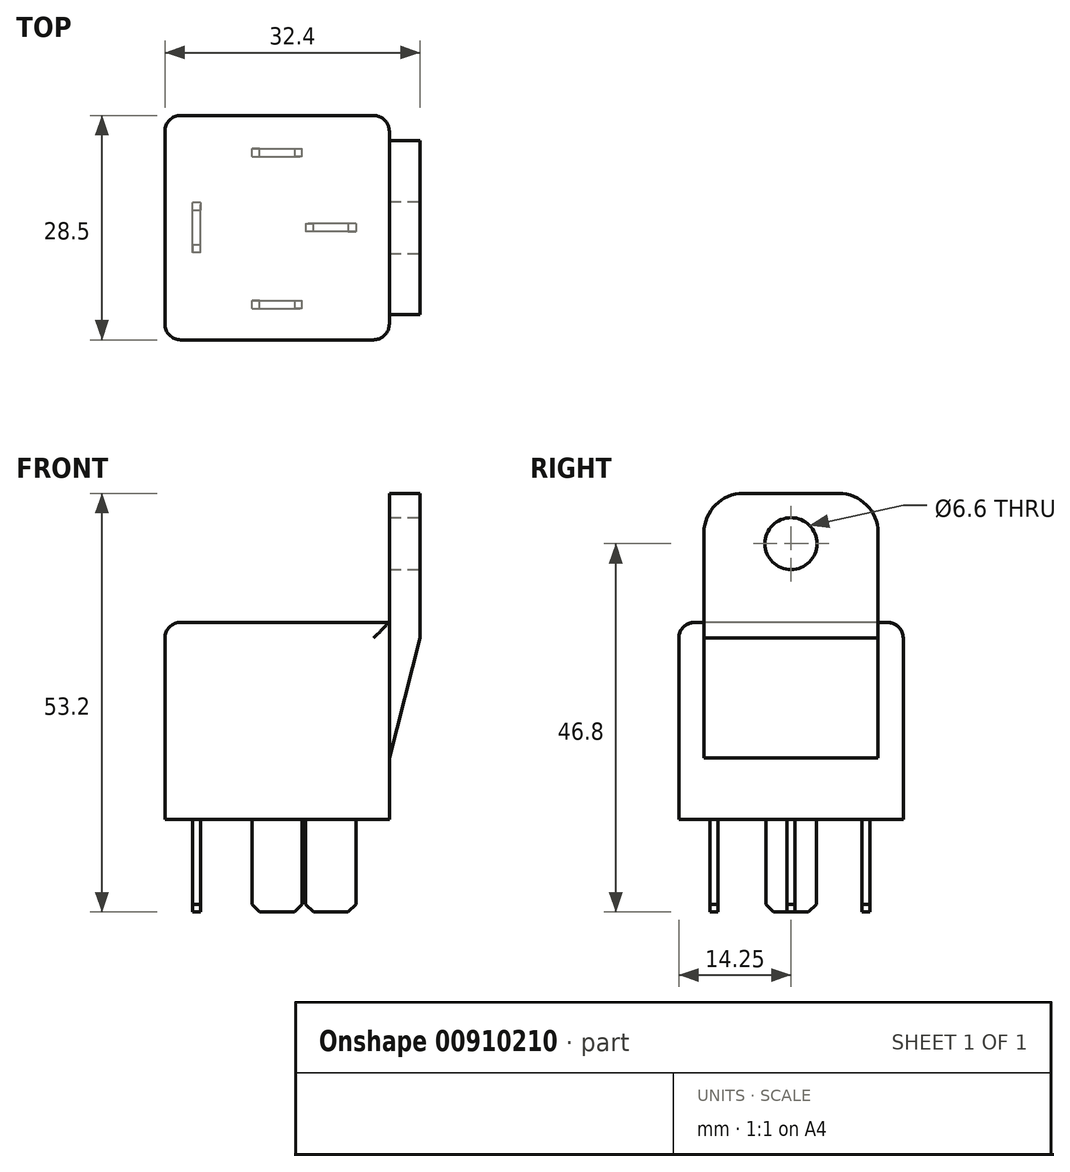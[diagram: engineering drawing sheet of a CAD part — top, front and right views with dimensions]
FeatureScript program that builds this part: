
annotation { "Feature Type Name" : "Feature", "Feature Type Description" : "" }
export const myFeature = defineFeature(function(context is Context, id is Id, definition is map)
    precondition{}
    {
        {
            var Q0;
            Q0=qCreatedBy(makeId("Top.planeOp"),FACE);
            var sketch = newSketch(context, id + "F0", { "sketchPlane" : qUnion([Q0])});
            skLineSegment(sketch, "E0.bottom", {"start": v(-14.25, 14.25) * mm, "end": v(14.25, 14.25) * mm});
            skLineSegment(sketch, "E0.top", {"start": v(-14.25, -14.25) * mm, "end": v(14.25, -14.25) * mm});
            skLineSegment(sketch, "E0.left", {"start": v(-14.25, 14.25) * mm, "end": v(-14.25, -14.25) * mm});
            skLineSegment(sketch, "E0.right", {"start": v(14.25, 14.25) * mm, "end": v(14.25, -14.25) * mm});
            skPoint(sketch, "E0.middle", {"position": v(0, 0) * mm});
            skSolve(sketch);
        }
        {
            var Q0;
            Q0 = qSketchRegion(id + "F0", true);
            extrude(context, id + "F1", {"entities" : qUnion([Q0]), "depth" : 25 * mm, "offsetDistance" : 25 * mm});
        }
        {
            var Q0;
            Q0=makeQuery(id+"F1.opExtrude","SWEPT_FACE",FACE,{"disambiguationData":[OSD([sQuery(id+"F0.wireOp",EDGE,"E0.top")])]});
            var sketch = newSketch(context, id + "F2", { "sketchPlane" : qUnion([Q0])});
            skLineSegment(sketch, "E1", {"start": v(14.25, 23) * mm, "end": v(18.15, 23) * mm});
            skLineSegment(sketch, "E2", {"start": v(18.15, 23) * mm, "end": v(14.25, 7.8) * mm});
            skSolve(sketch);
        }
        {
            var Q0;
            Q0 = qSketchRegion(id + "F2", true);
            var Q1;
            {var subQ0=sQuery(id+"F2.wireOp",EDGE,"E1");Q1=makeQuery(id+"F2.imprint","IMPRINT",FACE,{"disambiguationData":[TD([[makeQuery(id+"F2.imprint","IMPRINT",EDGE,{"derivedFrom":subQ0}),-1.0]])]});}
            extrude(context, id + "F3", {"entities" : qUnion([Q0, Q1]), "operationType" : NewBodyOperationType.ADD, "oppositeDirection" : true, "depth" : 25.3 * mm, "offsetDistance" : 25 * mm, "hasSecondDirection" : true, "secondDirectionOppositeDirection" : false, "secondDirectionDepth" : -3.2 * mm});
        }
        {
            var Q0;
            Q0=makeQuery(id+"F3.opExtrude","SWEPT_FACE",FACE,{"disambiguationData":[OSD([sQuery(id+"F2.wireOp",EDGE,"E1")])]});
            extrude(context, id + "F4", {"entities" : qUnion([Q0]), "operationType" : NewBodyOperationType.ADD, "depth" : 18.4 * mm, "offsetDistance" : 25 * mm});
        }
        {
            var Q0;
            {var subQ0=sQuery(id+"F2.wireOp",EDGE,"E1");Q0=makeQuery(id+"F4.opExtrude","CAP_EDGE",EDGE,{"disambiguationData":[OSD([subQ0]),TDD([makeQuery(id+"F3.opExtrude","CAP_EDGE",EDGE,{"disambiguationData":[OSD([subQ0])],"isStart":true})])],"isStart":false});}
            var Q1;
            {var subQ0=sQuery(id+"F2.wireOp",EDGE,"E1");Q1=makeQuery(id+"F4.opExtrude","CAP_EDGE",EDGE,{"disambiguationData":[OSD([subQ0]),TDD([makeQuery(id+"F3.opExtrude","CAP_EDGE",EDGE,{"disambiguationData":[OSD([subQ0])],"isStart":false})])],"isStart":false});}
            fillet(context, id + "F5", {"entities" : qUnion([Q0, Q1]), "radius" : 5 * mm, "tangentPropagation" : true, "allowEdgeOverflow" : false});
        }
        {
            var Q0;
            Q0=makeQuery(id+"F4.opExtrude","SWEPT_FACE",FACE,{"disambiguationData":[OSD([sQuery(id+"F2.wireOp",EDGE,"E1"),sQuery(id+"F2.wireOp",EDGE,"E2")])]});
            var sketch = newSketch(context, id + "F6", { "sketchPlane" : qUnion([Q0])});
            skCircle(sketch, "E3", {"center": v(0, 35) * mm, "radius": 3.3 * mm});
            skPoint(sketch, "E3.centerSnap0", {"position": v(0, 41.4) * mm});
            skSolve(sketch);
        }
        {
            var Q0;
            Q0 = qSketchRegion(id + "F6", true);
            extrude(context, id + "F7", {"entities" : qUnion([Q0]), "operationType" : NewBodyOperationType.REMOVE, "endBound" : BoundingType.THROUGH_ALL, "oppositeDirection" : true, "depth" : 25 * mm, "offsetDistance" : 25 * mm});
        }
        {
            var Q0;
            Q0=makeQuery(id+"F1.opExtrude","CAP_EDGE",EDGE,{"disambiguationData":[OSD([sQuery(id+"F0.wireOp",EDGE,"E0.bottom")])],"isStart":false});
            var Q1;
            Q1=makeQuery(id+"F1.opExtrude","CAP_EDGE",EDGE,{"disambiguationData":[OSD([sQuery(id+"F0.wireOp",EDGE,"E0.left")])],"isStart":false});
            var Q2;
            Q2=makeQuery(id+"F1.opExtrude","CAP_EDGE",EDGE,{"disambiguationData":[OSD([sQuery(id+"F0.wireOp",EDGE,"E0.top")])],"isStart":false});
            var Q3;
            Q3=makeQuery(id+"F1.opExtrude","SWEPT_EDGE",EDGE,{"disambiguationData":[OSD([sQuery(id+"F0.wireOp",EDGE,"E0.bottom"),sQuery(id+"F0.wireOp",EDGE,"E0.left")])]});
            var Q4;
            Q4=makeQuery(id+"F1.opExtrude","SWEPT_EDGE",EDGE,{"disambiguationData":[OSD([sQuery(id+"F0.wireOp",EDGE,"E0.top"),sQuery(id+"F0.wireOp",EDGE,"E0.left")])]});
            var Q5;
            Q5=makeQuery(id+"F1.opExtrude","SWEPT_EDGE",EDGE,{"disambiguationData":[OSD([sQuery(id+"F0.wireOp",EDGE,"E0.bottom"),sQuery(id+"F0.wireOp",EDGE,"E0.right")])]});
            var Q6;
            Q6=makeQuery(id+"F1.opExtrude","SWEPT_EDGE",EDGE,{"disambiguationData":[OSD([sQuery(id+"F0.wireOp",EDGE,"E0.top"),sQuery(id+"F0.wireOp",EDGE,"E0.right")])]});
            fillet(context, id + "F8", {"entities" : qUnion([Q0, Q1, Q2, Q3, Q4, Q5, Q6]), "radius" : 2 * mm, "tangentPropagation" : true, "allowEdgeOverflow" : false});
        }
        {
            var Q0;
            Q0=makeQuery(id+"F1.opExtrude","CAP_FACE",FACE,{"disambiguationData":[OSD([sQuery(id+"F0.wireOp",EDGE,"E0.bottom"),sQuery(id+"F0.wireOp",EDGE,"E0.top"),sQuery(id+"F0.wireOp",EDGE,"E0.left"),sQuery(id+"F0.wireOp",EDGE,"E0.right")])],"isStart":true});
            var sketch = newSketch(context, id + "F9", { "sketchPlane" : qUnion([Q0])});
            skLineSegment(sketch, "E4.bottom", {"start": v(-9.72, 3.2) * mm, "end": v(-10.72, 3.2) * mm});
            skLineSegment(sketch, "E4.top", {"start": v(-9.72, -3.2) * mm, "end": v(-10.72, -3.2) * mm});
            skLineSegment(sketch, "E4.left", {"start": v(-9.72, 3.2) * mm, "end": v(-9.72, -3.2) * mm});
            skLineSegment(sketch, "E4.right", {"start": v(-10.72, 3.2) * mm, "end": v(-10.72, -3.2) * mm});
            skPoint(sketch, "E4.middle", {"position": v(-10.22, 0) * mm});
            skPoint(sketch, "E4.middle.positionSnap0", {"position": v(-14.25, 0) * mm});
            skPoint(sketch, "E4.centerSnap0", {"position": v(-14.25, 0) * mm});
            skLineSegment(sketch, "E5.bottom", {"start": v(10, -0.5) * mm, "end": v(3.6, -0.5) * mm});
            skLineSegment(sketch, "E5.top", {"start": v(10, 0.5) * mm, "end": v(3.6, 0.5) * mm});
            skLineSegment(sketch, "E5.left", {"start": v(10, -0.5) * mm, "end": v(10, 0.5) * mm});
            skLineSegment(sketch, "E5.right", {"start": v(3.6, -0.5) * mm, "end": v(3.6, 0.5) * mm});
            skPoint(sketch, "E5.middle", {"position": v(6.8, 0) * mm});
            skPoint(sketch, "E5.middle.positionSnap0", {"position": v(14.25, 0) * mm});
            skPoint(sketch, "E5.centerSnap0", {"position": v(14.25, 0) * mm});
            skLineSegment(sketch, "E6.bottom", {"start": v(-3.2, -9) * mm, "end": v(3.2, -9) * mm});
            skLineSegment(sketch, "E6.top", {"start": v(-3.2, -10) * mm, "end": v(3.2, -10) * mm});
            skLineSegment(sketch, "E6.left", {"start": v(-3.2, -9) * mm, "end": v(-3.2, -10) * mm});
            skLineSegment(sketch, "E6.right", {"start": v(3.2, -9) * mm, "end": v(3.2, -10) * mm});
            skPoint(sketch, "E6.middle", {"position": v(0, -9.5) * mm});
            skLineSegment(sketch, "E7.bottom", {"start": v(-3.2, 10.27) * mm, "end": v(3.2, 10.27) * mm});
            skLineSegment(sketch, "E7.top", {"start": v(-3.2, 9.27) * mm, "end": v(3.2, 9.27) * mm});
            skLineSegment(sketch, "E7.left", {"start": v(-3.2, 10.27) * mm, "end": v(-3.2, 9.27) * mm});
            skLineSegment(sketch, "E7.right", {"start": v(3.2, 10.27) * mm, "end": v(3.2, 9.27) * mm});
            skPoint(sketch, "E7.middle", {"position": v(0, 9.77) * mm});
            skSolve(sketch);
        }
        {
            var Q0;
            Q0 = qSketchRegion(id + "F9", true);
            extrude(context, id + "F10", {"entities" : qUnion([Q0]), "operationType" : NewBodyOperationType.ADD, "depth" : 11.8 * mm, "offsetDistance" : 25 * mm});
        }
        {
            var Q0;
            Q0=makeQuery(id+"F10.opExtrude","CAP_EDGE",EDGE,{"disambiguationData":[OSD([sQuery(id+"F9.wireOp",EDGE,"E6.left")])],"isStart":false});
            var Q1;
            Q1=makeQuery(id+"F10.opExtrude","CAP_EDGE",EDGE,{"disambiguationData":[OSD([sQuery(id+"F9.wireOp",EDGE,"E6.right")])],"isStart":false});
            var Q2;
            Q2=makeQuery(id+"F10.opExtrude","CAP_EDGE",EDGE,{"disambiguationData":[OSD([sQuery(id+"F9.wireOp",EDGE,"E4.top")])],"isStart":false});
            var Q3;
            Q3=makeQuery(id+"F10.opExtrude","CAP_EDGE",EDGE,{"disambiguationData":[OSD([sQuery(id+"F9.wireOp",EDGE,"E4.bottom")])],"isStart":false});
            var Q4;
            Q4=makeQuery(id+"F10.opExtrude","CAP_EDGE",EDGE,{"disambiguationData":[OSD([sQuery(id+"F9.wireOp",EDGE,"E7.left")])],"isStart":false});
            var Q5;
            Q5=makeQuery(id+"F10.opExtrude","CAP_EDGE",EDGE,{"disambiguationData":[OSD([sQuery(id+"F9.wireOp",EDGE,"E7.right")])],"isStart":false});
            var Q6;
            Q6=makeQuery(id+"F10.opExtrude","CAP_EDGE",EDGE,{"disambiguationData":[OSD([sQuery(id+"F9.wireOp",EDGE,"E5.right")])],"isStart":false});
            var Q7;
            Q7=makeQuery(id+"F10.opExtrude","CAP_EDGE",EDGE,{"disambiguationData":[OSD([sQuery(id+"F9.wireOp",EDGE,"E5.left")])],"isStart":false});
            chamfer(context, id + "F11", {"entities" : qUnion([Q0, Q1, Q2, Q3, Q4, Q5, Q6, Q7]), "width" : 1 * mm, "tangentPropagation" : true});
        }
    });
